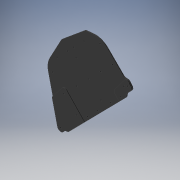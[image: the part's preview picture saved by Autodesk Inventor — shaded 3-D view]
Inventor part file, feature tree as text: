
AUTODESK INVENTOR PART (.ipt)
format: ipt  version: 2019.3 (Build 233278000, 278)  size: 247,296 bytes
history: native  units: mm
features: reference x23, other x15, extrude x3, fillet x3, sketch x3
ambient origin geometry x8: Origin, YZ Plane, XZ Plane, XY Plane, X Axis, Y Axis, Z Axis, Center Point
bodies: Body1 (feature_tree), Body2 (feature_tree), Body3 (feature_tree)
feature tree (47):
  other  "Sideplate"
  extrude  "Extrusion1"  Depth=60.0mm
  fillet  "Fillet1"  Radius=10.0mm
  extrude  "Extrusion2"  Depth=10.0mm
  fillet  "Fillet2"  Radius=3.0mm
  extrude  "Extrusion3"  [1 undecoded]
  fillet  "Fillet3"  [1 undecoded]
  sketch  "Sketch1"  dims[d0=3.0mm d1=0.0mm d2=60.0mm d3=10.0mm]
  reference  "Reference1"
  reference  "Reference2"
  reference  "Reference3"
  reference  "Reference4"
  reference  "Reference5"
  reference  "Reference6"
  reference  "Reference7"
  reference  "Reference8"
  reference  "Reference9"
  reference  "Reference10"
  reference  "Reference11"
  reference  "Reference12"
  reference  "Reference13"
  reference  "Reference14"
  reference  "Reference15"
  reference  "Reference16"
  reference  "Reference17"
  reference  "Reference18"
  reference  "Reference19"
  reference  "Reference20"
  reference  "Reference21"
  sketch  "Sketch2"  dims[d4=3.0mm d5=0.0mm d6=10.0mm d7=3.0mm d8=0.0mm]
  reference  "Reference22"
  other  "ReinforcementBack"
  sketch  "Sketch3"  dims[d9=10.0mm]
  reference  "Reference23"
  other  "ReinforcementFront"
  other  "<userpath>\Desktop\3dprojects\OpenEmoto\MainFrame\Battery2\Assembly1.iam"
  other  "Assembly1.iam"
  other  "LowerCage:1"
  other  "SpacerSmall:2"
  other  "SpacerSmall:3"
  other  "SpacerBig:5"
  other  "SpacerBig:2"
  other  "SpacerBig:3"
  other  "SpacerBig:4"
  other  "SpacerBig:1"
  other  "SpacerSmall:5"
  other  "SpacerSmall:4"
note: 2 required parameter values undecoded (feature->parameter linkage not recoverable at this tier; creation-order binding heuristic only, values carry confidence <= 0.55)
